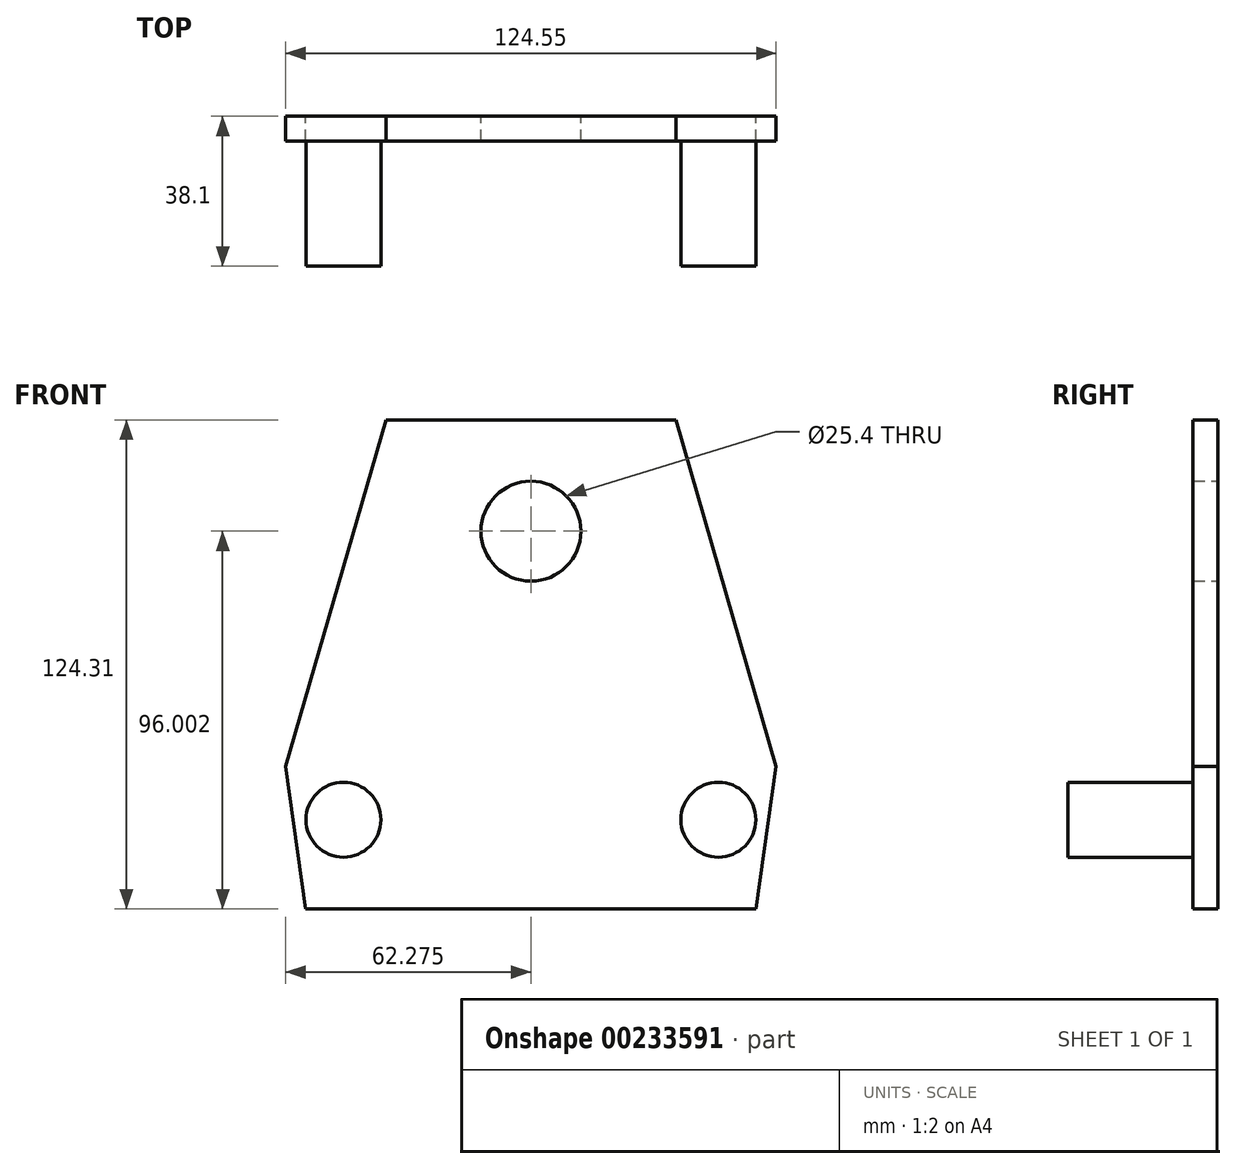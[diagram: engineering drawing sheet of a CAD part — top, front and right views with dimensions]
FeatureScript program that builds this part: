
annotation { "Feature Type Name" : "Feature", "Feature Type Description" : "" }
export const myFeature = defineFeature(function(context is Context, id is Id, definition is map)
    precondition{}
    {
        {
            var Q0;
            Q0=qCreatedBy(makeId("Front.planeOp"),FACE);
            var sketch = newSketch(context, id + "F0", { "sketchPlane" : qUnion([Q0])});
            skLineSegment(sketch, "E0", {"start": v(0, 0) * mm, "end": v(-95.25, 0) * mm, "construction": true});
            skCircle(sketch, "E1", {"center": v(-95.25, 0) * mm, "radius": 9.53 * mm});
            skCircle(sketch, "E2", {"center": v(0, 0) * mm, "radius": 9.53 * mm});
            skLineSegment(sketch, "E3", {"start": v(-47.63, 0) * mm, "end": v(-47.63, 101.6) * mm});
            skLineSegment(sketch, "E4", {"start": v(-47.63, 101.6) * mm, "end": v(-84.47, 101.6) * mm});
            skLineSegment(sketch, "E5", {"start": v(-84.47, 101.6) * mm, "end": v(-109.9, 13.53) * mm});
            skLineSegment(sketch, "E6", {"start": v(-109.9, 13.53) * mm, "end": v(-104.82, -22.7) * mm});
            skLineSegment(sketch, "E7", {"start": v(-104.82, -22.7) * mm, "end": v(19.16, -22.7) * mm});
            skLineSegment(sketch, "E8.MirrorCS", {"start": v(-47.63, 101.6) * mm, "end": v(-10.78, 101.6) * mm});
            skLineSegment(sketch, "E9.MirrorCS", {"start": v(-10.78, 101.6) * mm, "end": v(14.65, 13.53) * mm});
            skLineSegment(sketch, "E10.MirrorCS", {"start": v(14.65, 13.53) * mm, "end": v(9.57, -22.7) * mm});
            skCircle(sketch, "E11", {"center": v(-47.63, 73.3) * mm, "radius": 12.7 * mm});
            skSolve(sketch);
        }
        {
            var Q0;
            Q0=qSketchRegion(id+"F0",true);
            extrude(context, id + "F1", {"entities" : qUnion([Q0]), "depth" : 6.35 * mm});
        }
        {
            var Q0;
            Q0=makeQuery(id+"F0.imprint","IMPRINT",FACE,{"disambiguationData":[TD([[makeQuery(id+"F0.imprint","IMPRINT",EDGE,{"derivedFrom":sQuery(id+"F0.wireOp",EDGE,"E1")}),1.0]])]});
            var Q1;
            Q1=makeQuery(id+"F0.imprint","IMPRINT",FACE,{"disambiguationData":[TD([[makeQuery(id+"F0.imprint","IMPRINT",EDGE,{"derivedFrom":sQuery(id+"F0.wireOp",EDGE,"E2")}),1.0]])]});
            extrude(context, id + "F2", {"entities" : qUnion([Q0, Q1]), "operationType" : NewBodyOperationType.ADD, "depth" : 38.1 * mm});
        }
    });
